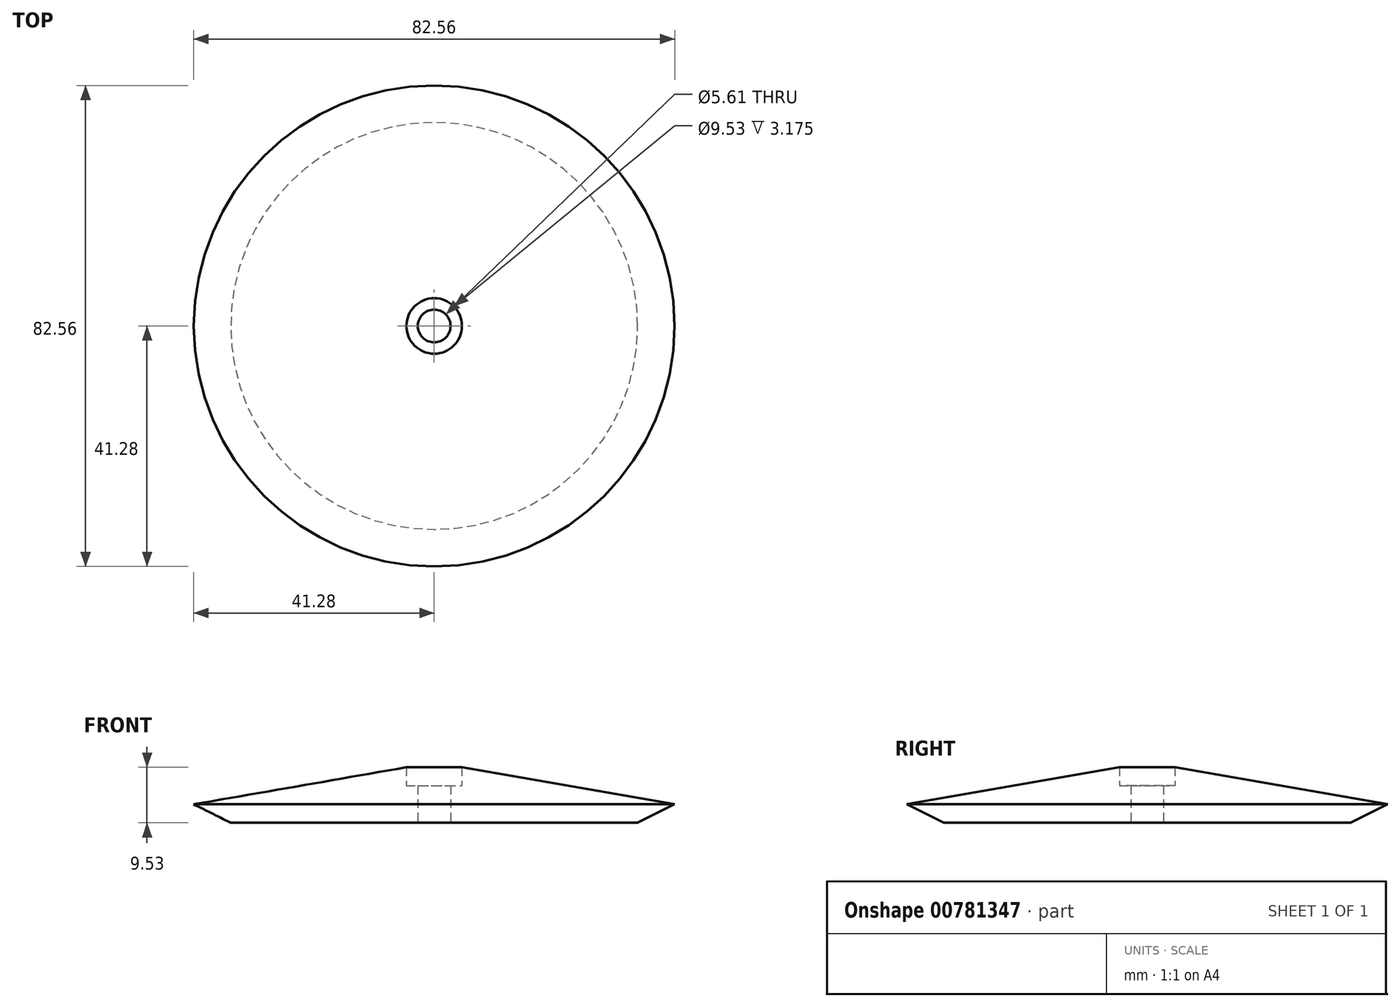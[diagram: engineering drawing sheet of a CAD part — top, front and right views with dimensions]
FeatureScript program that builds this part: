
annotation { "Feature Type Name" : "Feature", "Feature Type Description" : "" }
export const myFeature = defineFeature(function(context is Context, id is Id, definition is map)
    precondition{}
    {
        {
            var Q0;
            Q0=qCreatedBy(makeId("Front.planeOp"),FACE);
            var sketch = newSketch(context, id + "F0", { "sketchPlane" : qUnion([Q0])});
            skLineSegment(sketch, "E0", {"start": v(-2.8, 0) * mm, "end": v(-2.8, 6.35) * mm});
            skLineSegment(sketch, "E1", {"start": v(-2.8, 6.35) * mm, "end": v(-4.76, 6.35) * mm});
            skLineSegment(sketch, "E2", {"start": v(-4.76, 6.35) * mm, "end": v(-4.76, 9.53) * mm});
            skLineSegment(sketch, "E3", {"start": v(-4.76, 9.53) * mm, "end": v(-41.28, 3.17) * mm});
            skLineSegment(sketch, "E4", {"start": v(-41.28, 3.17) * mm, "end": v(-34.93, 0) * mm});
            skLineSegment(sketch, "E5", {"start": v(-34.93, 0) * mm, "end": v(-2.8, 0) * mm});
            skLineSegment(sketch, "E6", {"start": v(0, 0) * mm, "end": v(0, 29.7) * mm, "construction": true});
            skSolve(sketch);
        }
        {
            var Q0;
            Q0=makeQuery(id+"F0.imprint","IMPRINT",FACE,{"disambiguationData":[TD([[makeQuery(id+"F0.imprint","IMPRINT",EDGE,{"derivedFrom":sQuery(id+"F0.wireOp",EDGE,"E0")}),1.0]])]});
            var Q1;
            Q1=sQuery(id+"F0.wireOp",EDGE,"E6");
            revolve(context, id + "F1", {"surfaceOperationType" : NewSurfaceOperationType.NEW, "entities" : qUnion([Q0]), "axis" : qUnion([Q1]), "revolveType" : RevolveType.FULL});
        }
    });
